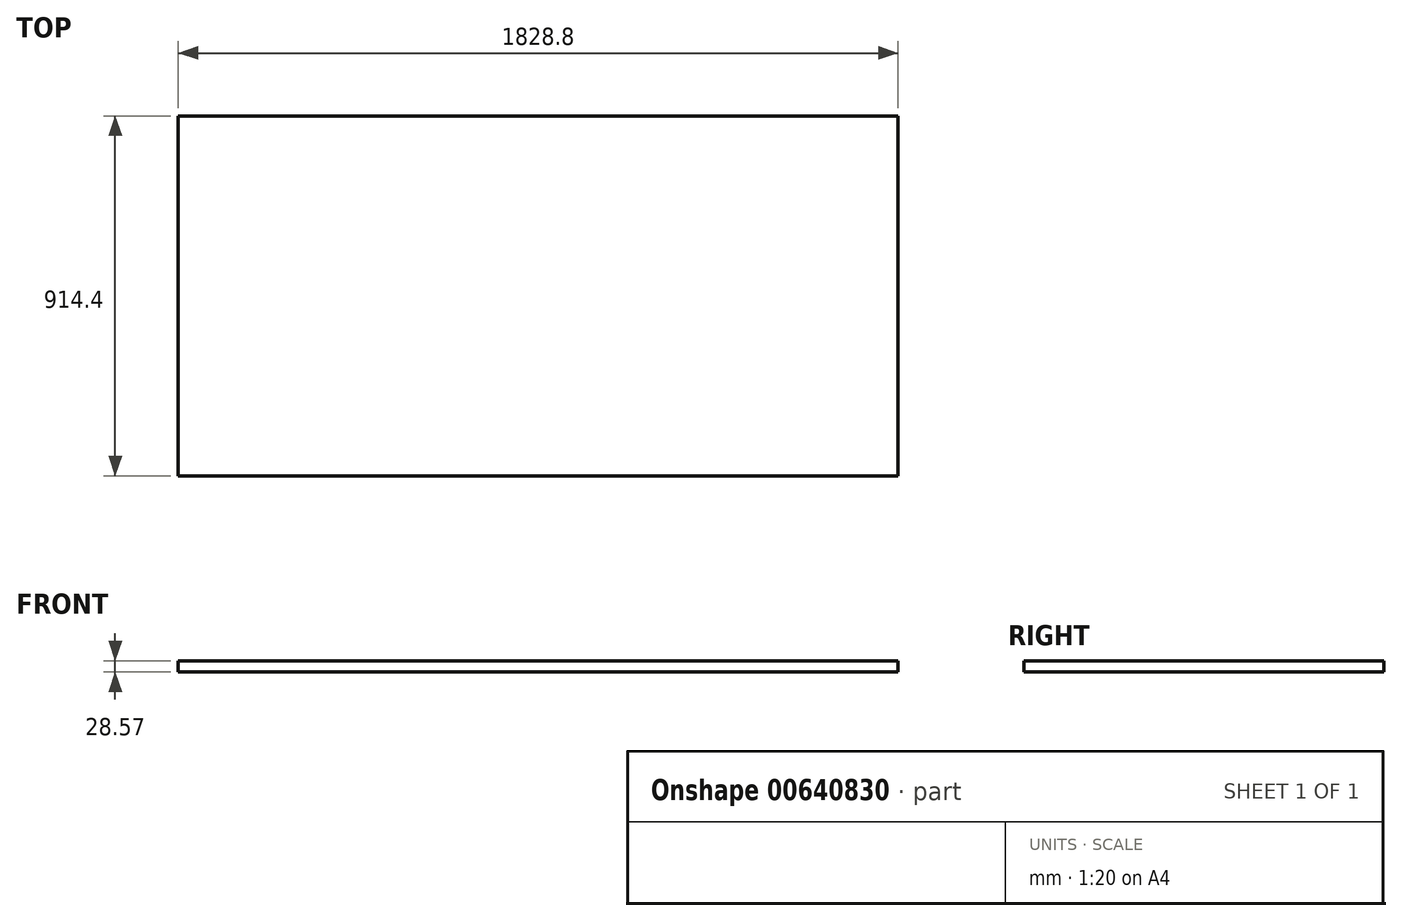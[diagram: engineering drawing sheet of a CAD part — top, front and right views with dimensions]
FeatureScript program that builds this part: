
annotation { "Feature Type Name" : "Feature", "Feature Type Description" : "" }
export const myFeature = defineFeature(function(context is Context, id is Id, definition is map)
    precondition{}
    {
        {
            var Q0;
            Q0=qCreatedBy(makeId("Top.planeOp"),FACE);
            var sketch = newSketch(context, id + "F0", { "sketchPlane" : qUnion([Q0])});
            skLineSegment(sketch, "E0.bottom", {"start": v(914.4, 457.2) * mm, "end": v(-914.4, 457.2) * mm});
            skLineSegment(sketch, "E0.top", {"start": v(914.4, -457.2) * mm, "end": v(-914.4, -457.2) * mm});
            skLineSegment(sketch, "E0.left", {"start": v(914.4, 457.2) * mm, "end": v(914.4, -457.2) * mm});
            skLineSegment(sketch, "E0.right", {"start": v(-914.4, 457.2) * mm, "end": v(-914.4, -457.2) * mm});
            skPoint(sketch, "E0.middle", {"position": v(0, 0) * mm});
            skSolve(sketch);
        }
        {
            var Q0;
            Q0=makeQuery(id+"F0.imprint","IMPRINT",FACE,{"disambiguationData":[TD([[makeQuery(id+"F0.imprint","IMPRINT",EDGE,{"derivedFrom":sQuery(id+"F0.wireOp",EDGE,"E0.bottom")}),1.0]])]});
            extrude(context, id + "F1", {"entities" : qUnion([Q0]), "depth" : 28.57 * mm, "offsetDistance" : 25.4 * mm});
        }
    });
